# Revit family: Drinking_Fountain-Oasis-Aqua_Pointe_Sports_Bottle_Filler-MCRSBF
name_source: partatom
category: Plumbing Fixtures
revit_build: Autodesk Revit MEP 2013 (Build: 20130531_2115(x64)
units: mm (PartAtom-declared; Revit-internal decimal feet)

## types (1)
- MCRSBF
    Apparent Load = 7 VA
    Base Rate = 0 GPM
    Chiller = No
    Cold Water Connector 1 = Cold Water Connection 1
    Cold Water Connector 2 = Cold Water Connection 2
    Compression HP = 0 VA
    Default Elevation = 2' - 3"
    Description = Aqua Pointe Sports Bottle Filler
    Finish = Metal - Oasis International - Brushed Stainless Steel - Exterior Finish
    Full Load Amps = 0 A
    Manufacturer = Oasis International
    Manufacturer Fax Number = (614)322-4557
    Metal Finish = Metal - Oasis International - Brushed Stainless Steel - Exterior Finish
    Model = MCRSBF
    Number of Poles = 1
    Power Factor = 1
    Product Name = Non Refrigerated, Bi Level Radii Fountain w/ Integrated Sports Bottle Filler
    Rated Capacity = 0 GPM
    Rated Watts = 7 W
    Sanitary Connector 1 = Sanitary Connection 1
    Sanitary Connector 2 = Sanitary Connection 2
    URL = http://www.oasiscoolers.com
    Voltage = 115 V
    Width = 3' - 2 3/4"

## geometry (parser evidence)
native form markers: Blend x14, Sweep x16
no freeform markers — native parametric forms only
